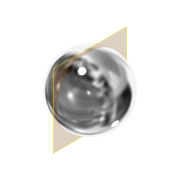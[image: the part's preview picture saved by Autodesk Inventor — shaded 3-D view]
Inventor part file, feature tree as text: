
AUTODESK INVENTOR PART (.ipt)
format: ipt  version: 2019.4 (Build 234330000, 330)  size: 127,488 bytes
history: native  units: mm
features: sketch x2, revolve x1, plane x1, extrude x1, other x1
ambient origin geometry x8: Origin, YZ Plane, XZ Plane, XY Plane, X Axis, Y Axis, Z Axis, Center Point
bodies: Volumenkörper1 (feature_tree)
feature tree (6):
  revolve  "Umdrehung1"
  plane  "Work Plane1"
  extrude  "Extrusion1"  TaperAngle=90.0deg  [1 undecoded]
  sketch  "Skizze1"  dims[d0=5.0mm d1=90.0deg]
  other  "Work Point1"
  sketch  "Sketch2"  dims[d8=0.1mm d9=0.0mm]
note: 1 required parameter value undecoded (feature->parameter linkage not recoverable at this tier; creation-order binding heuristic only, values carry confidence <= 0.55)
